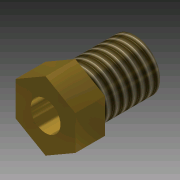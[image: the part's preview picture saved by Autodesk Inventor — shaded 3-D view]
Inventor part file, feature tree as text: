
AUTODESK INVENTOR PART (.ipt)
format: ipt  version: 2011 (Build 150239000, 239)  size: 95,744 bytes
history: native  units: in
note: dims shown in document units (in); Inventor stores cm internally (conversion verified against a paired STEP export)
features: extrude x3, sketch x3, thread x1
ambient origin geometry x8: Origin, YZ Plane, XZ Plane, XY Plane, X Axis, Y Axis, Z Axis, Center Point
bodies: Solid1 (feature_tree)
feature tree (7):
  extrude  "Extrusion1"  Depth=0.5in TaperAngle=0.0deg
  thread  "Thread1"  [1 undecoded]
  extrude  "Extrusion2"  TaperAngle=0.0deg  [1 undecoded]
  extrude  "Extrusion5"  Depth=0.25in
  sketch  "Sketch1"  dims[d0=0.425in d1=0.5in d2=0.0in d3=1.0in d4=0.0in]
  sketch  "Sketch2"  dims[d5=0.5in d6=0.0in]
  sketch  "Sketch5"  dims[d7=0.25in d8=0.0in d14=0.25in d15=1.0in d16=0.0in]
note: 2 required parameter values undecoded (feature->parameter linkage not recoverable at this tier; creation-order binding heuristic only, values carry confidence <= 0.55)
